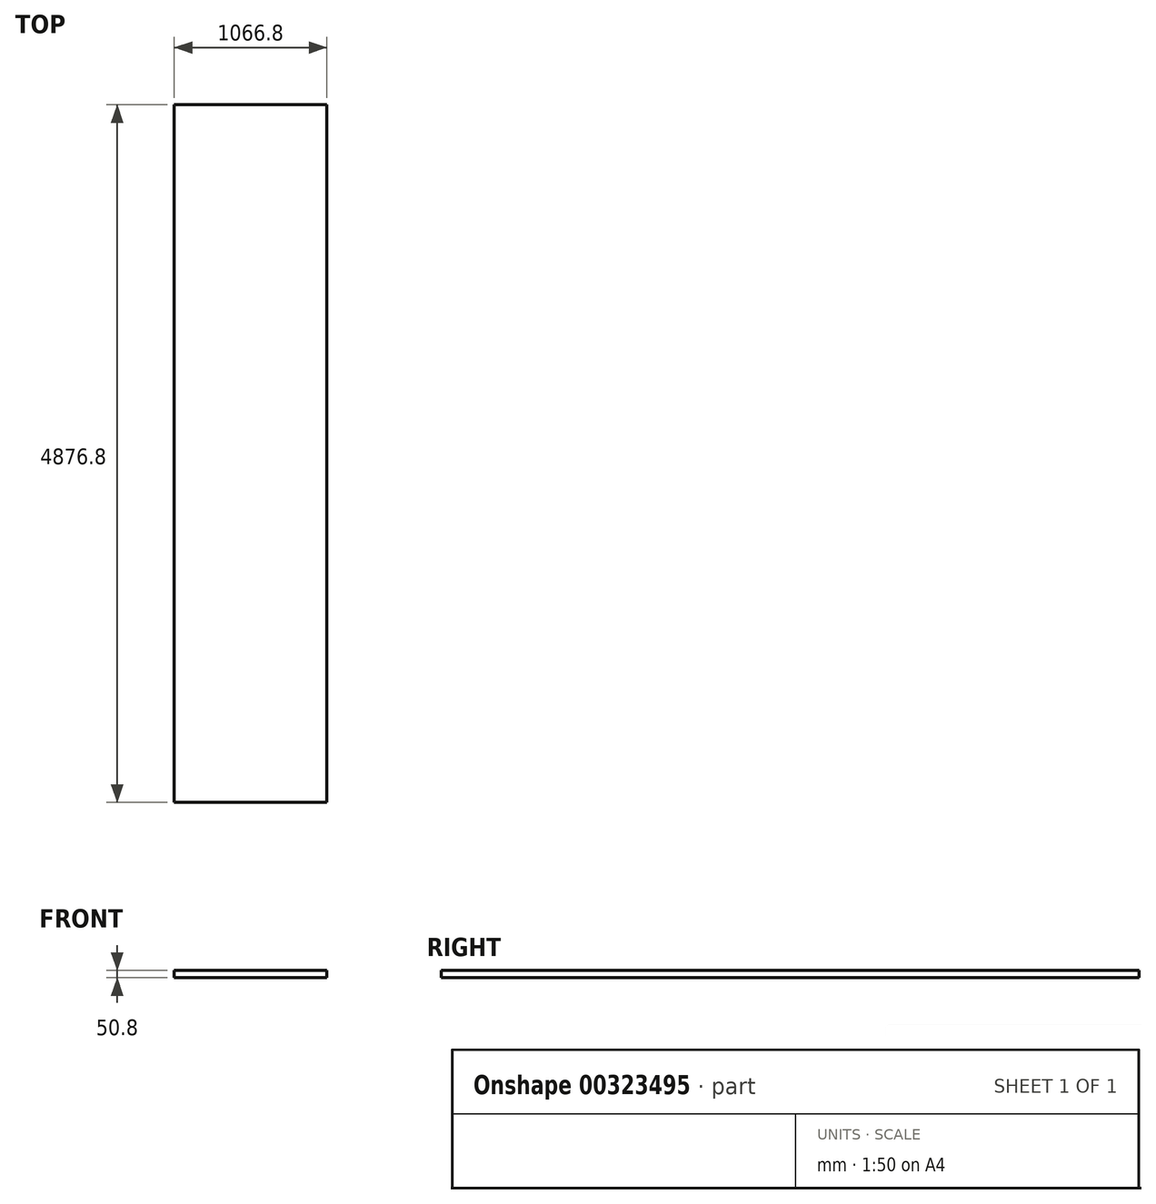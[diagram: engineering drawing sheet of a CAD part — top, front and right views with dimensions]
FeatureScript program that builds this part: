
annotation { "Feature Type Name" : "Feature", "Feature Type Description" : "" }
export const myFeature = defineFeature(function(context is Context, id is Id, definition is map)
    precondition{}
    {
        {
            var Q0;
            Q0=qCreatedBy(makeId("Top.planeOp"),FACE);
            var sketch = newSketch(context, id + "F0", { "sketchPlane" : qUnion([Q0])});
            skLineSegment(sketch, "E0.bottom", {"start": v(533.4, 2438.4) * mm, "end": v(-533.4, 2438.4) * mm});
            skLineSegment(sketch, "E0.top", {"start": v(533.4, -2438.4) * mm, "end": v(-533.4, -2438.4) * mm});
            skLineSegment(sketch, "E0.left", {"start": v(533.4, 2438.4) * mm, "end": v(533.4, -2438.4) * mm});
            skLineSegment(sketch, "E0.right", {"start": v(-533.4, 2438.4) * mm, "end": v(-533.4, -2438.4) * mm});
            skPoint(sketch, "E0.middle", {"position": v(0, 0) * mm});
            skSolve(sketch);
        }
        {
            var Q0;
            Q0=makeQuery(id+"F0.imprint","IMPRINT",FACE,{"disambiguationData":[TD([[makeQuery(id+"F0.imprint","IMPRINT",EDGE,{"derivedFrom":sQuery(id+"F0.wireOp",EDGE,"E0.bottom")}),1.0]])]});
            extrude(context, id + "F1", {"entities" : qUnion([Q0]), "depth" : 50.8 * mm});
        }
    });
